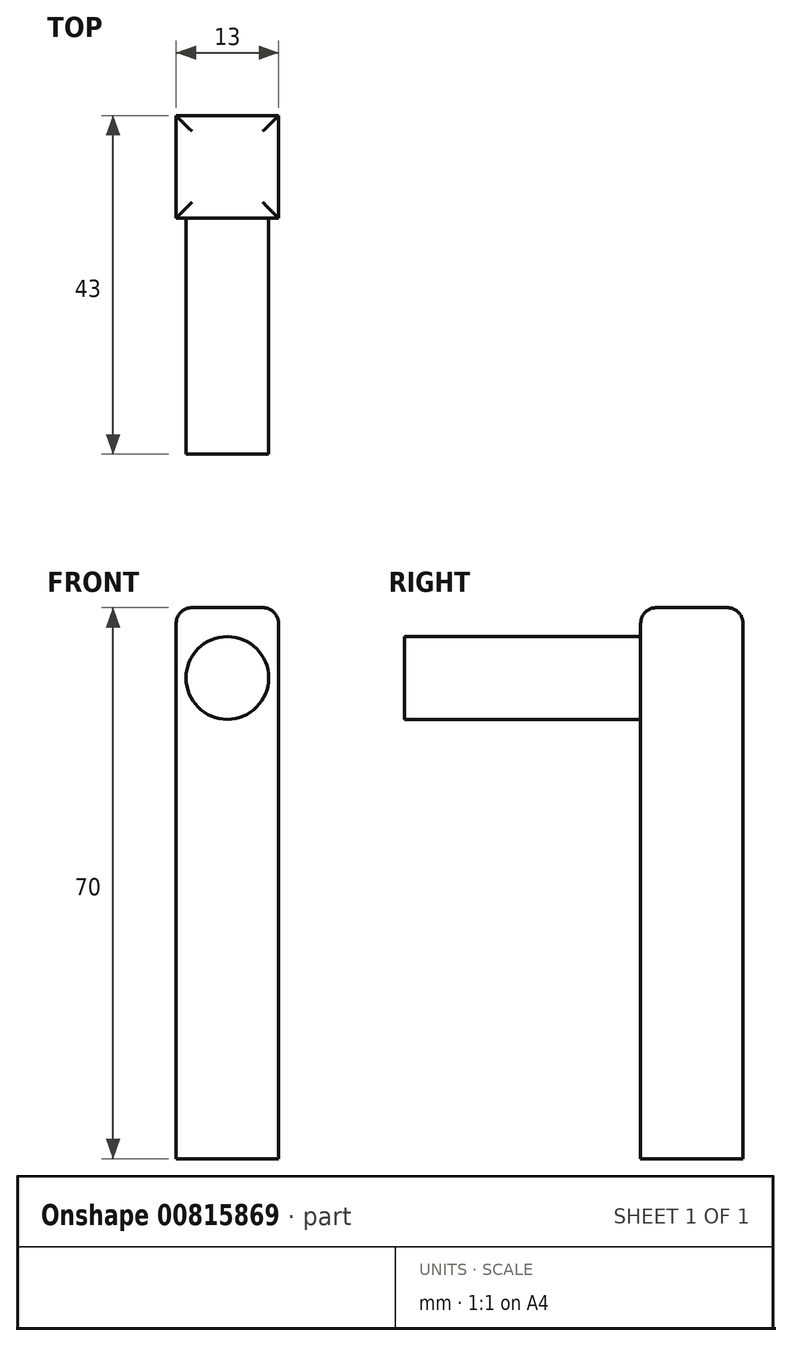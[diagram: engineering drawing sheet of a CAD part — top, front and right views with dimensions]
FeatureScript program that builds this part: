
annotation { "Feature Type Name" : "Feature", "Feature Type Description" : "" }
export const myFeature = defineFeature(function(context is Context, id is Id, definition is map)
    precondition{}
    {
        {
            var Q0;
            Q0=qCreatedBy(makeId("Top.planeOp"),FACE);
            var sketch = newSketch(context, id + "F0", { "sketchPlane" : qUnion([Q0])});
            skLineSegment(sketch, "E0.bottom", {"start": v(-6.5, 6.5) * mm, "end": v(6.5, 6.5) * mm});
            skLineSegment(sketch, "E0.top", {"start": v(-6.5, -6.5) * mm, "end": v(6.5, -6.5) * mm});
            skLineSegment(sketch, "E0.left", {"start": v(-6.5, 6.5) * mm, "end": v(-6.5, -6.5) * mm});
            skLineSegment(sketch, "E0.right", {"start": v(6.5, 6.5) * mm, "end": v(6.5, -6.5) * mm});
            skPoint(sketch, "E0.middle", {"position": v(0, 0) * mm});
            skSolve(sketch);
        }
        {
            var Q0;
            Q0 = qSketchRegion(id + "F0", true);
            extrude(context, id + "F1", {"entities" : qUnion([Q0]), "depth" : 70 * mm, "offsetDistance" : 25 * mm});
        }
        {
            var Q0;
            Q0=makeQuery(id+"F1.opExtrude","CAP_FACE",FACE,{"disambiguationData":[OSD([sQuery(id+"F0.wireOp",EDGE,"E0.bottom"),sQuery(id+"F0.wireOp",EDGE,"E0.top"),sQuery(id+"F0.wireOp",EDGE,"E0.left"),sQuery(id+"F0.wireOp",EDGE,"E0.right")])],"isStart":false});
            fillet(context, id + "F2", {"entities" : qUnion([Q0]), "radius" : 2 * mm, "tangentPropagation" : true, "allowEdgeOverflow" : false});
        }
        {
            var Q0;
            Q0=makeQuery(id+"F1.opExtrude","SWEPT_FACE",FACE,{"disambiguationData":[OSD([sQuery(id+"F0.wireOp",EDGE,"E0.top")])]});
            var sketch = newSketch(context, id + "F3", { "sketchPlane" : qUnion([Q0])});
            skCircle(sketch, "E1", {"center": v(0, 61.07) * mm, "radius": 5.25 * mm});
            skSolve(sketch);
        }
        {
            var Q0;
            Q0=makeQuery(id+"F3.imprint","IMPRINT",FACE,{"disambiguationData":[TD([[makeQuery(id+"F3.imprint","IMPRINT",EDGE,{"derivedFrom":sQuery(id+"F3.wireOp",EDGE,"E1")}),1.0]])]});
            extrude(context, id + "F4", {"entities" : qUnion([Q0]), "operationType" : NewBodyOperationType.ADD, "depth" : 30 * mm, "offsetDistance" : 25 * mm});
        }
    });
